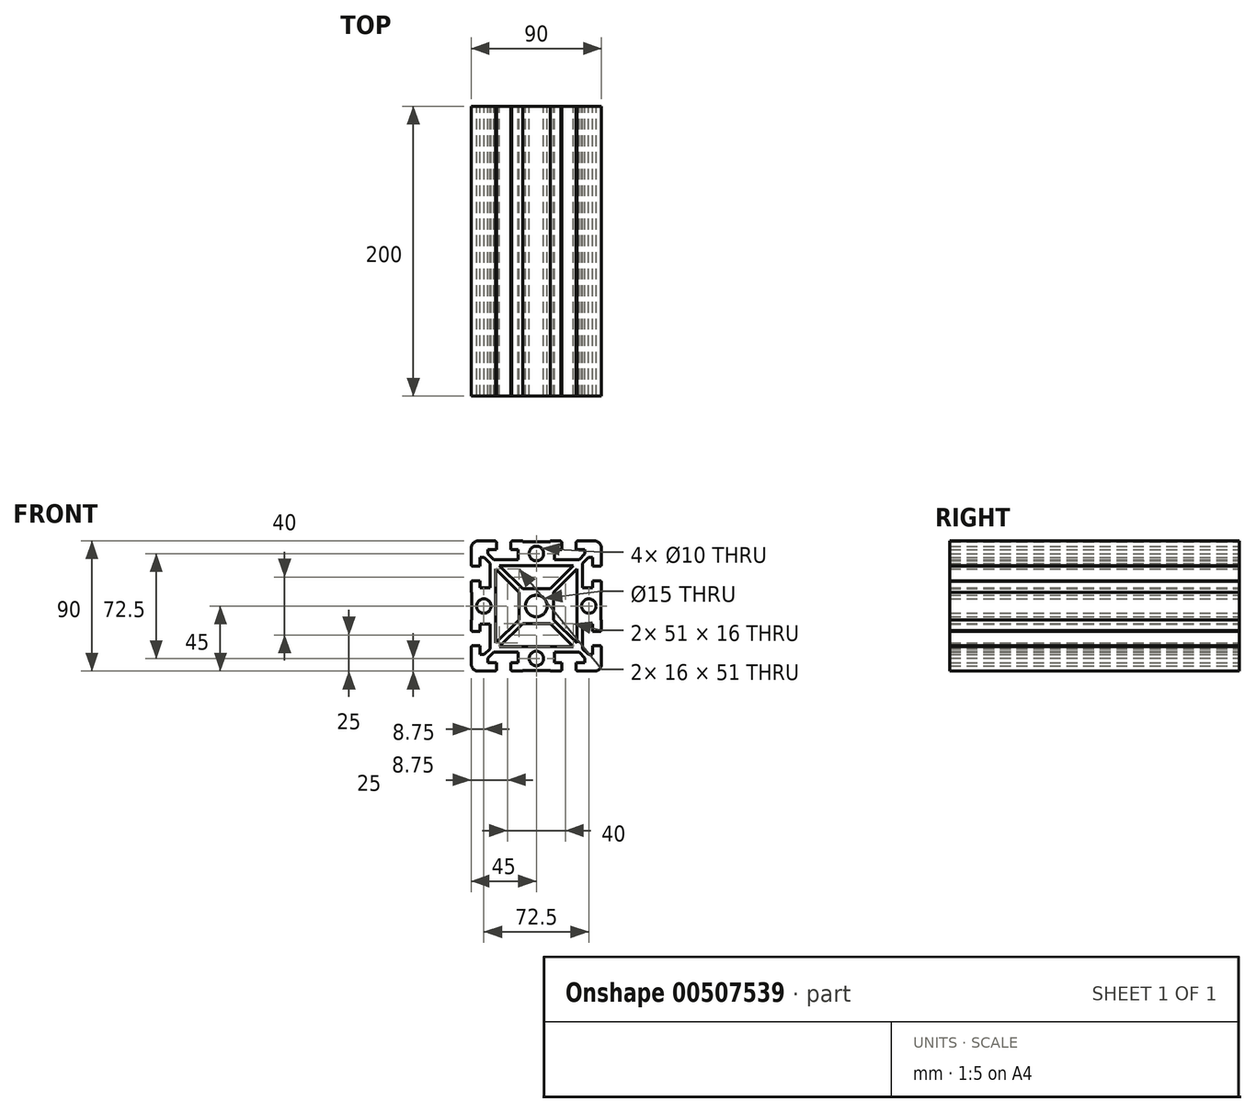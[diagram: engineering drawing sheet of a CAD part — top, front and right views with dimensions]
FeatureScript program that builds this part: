
annotation { "Feature Type Name" : "Feature", "Feature Type Description" : "" }
export const myFeature = defineFeature(function(context is Context, id is Id, definition is map)
    precondition{}
    {
        {
            var Q0;
            Q0=qCreatedBy(makeId("Front.planeOp"),FACE);
            var sketch = newSketch(context, id + "F0", { "sketchPlane" : qUnion([Q0])});
            skLineSegment(sketch, "E0", {"start": v(28, 45) * mm, "end": v(28, 44.5) * mm});
            skLineSegment(sketch, "E1", {"start": v(28, 44.5) * mm, "end": v(27.5, 44.5) * mm});
            skLineSegment(sketch, "E2", {"start": v(27.5, 44.5) * mm, "end": v(27.5, 39) * mm});
            skLineSegment(sketch, "E3", {"start": v(27.5, 39) * mm, "end": v(33.5, 39) * mm});
            skLineSegment(sketch, "E4", {"start": v(33.5, 39) * mm, "end": v(33.5, 36) * mm});
            skLineSegment(sketch, "E5", {"start": v(33.5, 36) * mm, "end": v(29.5, 32) * mm});
            skLineSegment(sketch, "E6", {"start": v(29.5, 32) * mm, "end": v(12.5, 32) * mm});
            skLineSegment(sketch, "E7", {"start": v(12.5, 32) * mm, "end": v(12.5, 39) * mm});
            skLineSegment(sketch, "E8", {"start": v(12.5, 39) * mm, "end": v(17.5, 39) * mm});
            skLineSegment(sketch, "E9", {"start": v(17.5, 39) * mm, "end": v(17.5, 44.5) * mm});
            skLineSegment(sketch, "E10", {"start": v(17.5, 44.5) * mm, "end": v(17, 44.5) * mm});
            skLineSegment(sketch, "E11", {"start": v(17, 44.5) * mm, "end": v(17, 45) * mm});
            skLineSegment(sketch, "E12", {"start": v(45, 28) * mm, "end": v(44.5, 28) * mm});
            skLineSegment(sketch, "E13", {"start": v(44.5, 28) * mm, "end": v(44.5, 27.5) * mm});
            skLineSegment(sketch, "E14", {"start": v(44.5, 27.5) * mm, "end": v(39, 27.5) * mm});
            skLineSegment(sketch, "E15", {"start": v(39, 27.5) * mm, "end": v(39, 33.5) * mm});
            skLineSegment(sketch, "E16", {"start": v(39, 33.5) * mm, "end": v(36, 33.5) * mm});
            skLineSegment(sketch, "E17", {"start": v(36, 33.5) * mm, "end": v(32, 29.5) * mm});
            skLineSegment(sketch, "E18", {"start": v(32, 29.5) * mm, "end": v(32, 12.5) * mm});
            skLineSegment(sketch, "E19", {"start": v(32, 12.5) * mm, "end": v(39, 12.5) * mm});
            skLineSegment(sketch, "E20", {"start": v(39, 12.5) * mm, "end": v(39, 17.5) * mm});
            skLineSegment(sketch, "E21", {"start": v(39, 17.5) * mm, "end": v(44.5, 17.5) * mm});
            skLineSegment(sketch, "E22", {"start": v(44.5, 17.5) * mm, "end": v(44.5, 17) * mm});
            skLineSegment(sketch, "E23", {"start": v(44.5, 17) * mm, "end": v(45, 17) * mm});
            skLineSegment(sketch, "E24", {"start": v(45, 28) * mm, "end": v(45, 40) * mm});
            skLineSegment(sketch, "E25", {"start": v(28, 45) * mm, "end": v(40, 45) * mm});
            skPoint(sketch, "E26.visualSharp", {"position": v(45, 45) * mm});
            skArc(sketch, "E26.filletArc", {"start": v(45, 40) * mm, "mid": v(43.54, 43.54) * mm, "end": v(40, 45) * mm});
            skLineSegment(sketch, "E27", {"start": v(17, 45) * mm, "end": v(9.5, 45) * mm});
            skLineSegment(sketch, "E28", {"start": v(9.5, 45) * mm, "end": v(9.5, 44.5) * mm});
            skLineSegment(sketch, "E29", {"start": v(9.5, 44.5) * mm, "end": v(0, 44.5) * mm});
            skLineSegment(sketch, "E30", {"start": v(0, 44.5) * mm, "end": v(0, 41.25) * mm});
            skLineSegment(sketch, "E31", {"start": v(45, 17) * mm, "end": v(45, 9.5) * mm});
            skLineSegment(sketch, "E32", {"start": v(45, 9.5) * mm, "end": v(44.5, 9.5) * mm});
            skLineSegment(sketch, "E33", {"start": v(44.5, 9.5) * mm, "end": v(44.5, 0) * mm});
            skLineSegment(sketch, "E34", {"start": v(44.5, 0) * mm, "end": v(41.25, 0) * mm});
            skLineSegment(sketch, "E35.bottom", {"start": v(7.5, 0) * mm, "end": v(12, 0) * mm});
            skLineSegment(sketch, "E35.top", {"start": v(0, 28) * mm, "end": v(25.5, 28) * mm});
            skLineSegment(sketch, "E35.right", {"start": v(28, 0) * mm, "end": v(28, 25.5) * mm});
            skLineSegment(sketch, "E36.top", {"start": v(0, 12) * mm, "end": v(9.5, 12) * mm});
            skLineSegment(sketch, "E36.left", {"start": v(0, 7.5) * mm, "end": v(0, 12) * mm});
            skLineSegment(sketch, "E36.right", {"start": v(12, 0) * mm, "end": v(12, 9.5) * mm});
            skArc(sketch, "E37", {"start": v(7.5, 0) * mm, "mid": v(5.3, 5.3) * mm, "end": v(0, 7.5) * mm});
            skLineSegment(sketch, "E38", {"start": v(25.5, 28) * mm, "end": v(9.5, 12) * mm});
            skLineSegment(sketch, "E39", {"start": v(28, 25.5) * mm, "end": v(12, 9.5) * mm});
            skLineSegment(sketch, "E40.trimOffspring", {"start": v(12, 0) * mm, "end": v(7.5, 0) * mm});
            skLineSegment(sketch, "E41.trimOffspring", {"start": v(0, 12) * mm, "end": v(0, 7.5) * mm});
            skArc(sketch, "E42", {"start": v(41.25, 0) * mm, "mid": v(36.25, 5) * mm, "end": v(31.25, 0) * mm});
            skArc(sketch, "E43", {"start": v(0, 31.25) * mm, "mid": v(5, 36.25) * mm, "end": v(0, 41.25) * mm});
            skLineSegment(sketch, "E44.trimOffspring", {"start": v(0, 31.25) * mm, "end": v(0, 28) * mm});
            skLineSegment(sketch, "E45.trimOffspring", {"start": v(31.25, 0) * mm, "end": v(28, 0) * mm});
            skLineSegment(sketch, "E46.1.0", {"start": v(-28, 0) * mm, "end": v(-28, 25.5) * mm});
            skLineSegment(sketch, "E46.1.1", {"start": v(0, 28) * mm, "end": v(-25.5, 28) * mm});
            skPoint(sketch, "E46.1.2", {"position": v(-45, 45) * mm});
            skArc(sketch, "E46.1.3", {"start": v(0, 41.25) * mm, "mid": v(-5, 36.25) * mm, "end": v(0, 31.25) * mm});
            skLineSegment(sketch, "E46.1.4", {"start": v(-25.5, 28) * mm, "end": v(-9.5, 12) * mm});
            skLineSegment(sketch, "E46.1.5", {"start": v(-44.5, 9.5) * mm, "end": v(-44.5, 0) * mm});
            skLineSegment(sketch, "E46.1.6", {"start": v(-28, 25.5) * mm, "end": v(-12, 9.5) * mm});
            skLineSegment(sketch, "E46.1.7", {"start": v(-28, 45) * mm, "end": v(-40, 45) * mm});
            skLineSegment(sketch, "E46.1.8", {"start": v(-32, 29.5) * mm, "end": v(-32, 12.5) * mm});
            skArc(sketch, "E46.1.9", {"start": v(-31.25, 0) * mm, "mid": v(-36.25, 5) * mm, "end": v(-41.25, 0) * mm});
            skLineSegment(sketch, "E46.1.10", {"start": v(-9.5, 44.5) * mm, "end": v(0, 44.5) * mm});
            skLineSegment(sketch, "E46.1.11", {"start": v(-12.5, 32) * mm, "end": v(-12.5, 39) * mm});
            skLineSegment(sketch, "E46.1.12", {"start": v(-12, 0) * mm, "end": v(-12, 9.5) * mm});
            skLineSegment(sketch, "E46.1.13", {"start": v(-45, 17) * mm, "end": v(-45, 9.5) * mm});
            skArc(sketch, "E46.1.14", {"start": v(-40, 45) * mm, "mid": v(-43.54, 43.54) * mm, "end": v(-45, 40) * mm});
            skArc(sketch, "E46.1.15", {"start": v(0, 7.5) * mm, "mid": v(-5.3, 5.3) * mm, "end": v(-7.5, 0) * mm});
            skLineSegment(sketch, "E46.1.16", {"start": v(-45, 28) * mm, "end": v(-45, 40) * mm});
            skLineSegment(sketch, "E46.1.17", {"start": v(0, 12) * mm, "end": v(-9.5, 12) * mm});
            skLineSegment(sketch, "E46.1.18", {"start": v(-17, 45) * mm, "end": v(-9.5, 45) * mm});
            skLineSegment(sketch, "E46.1.19", {"start": v(-32, 12.5) * mm, "end": v(-39, 12.5) * mm});
            skLineSegment(sketch, "E46.1.20", {"start": v(-29.5, 32) * mm, "end": v(-12.5, 32) * mm});
            skLineSegment(sketch, "E46.1.21", {"start": v(-12.5, 39) * mm, "end": v(-17.5, 39) * mm});
            skLineSegment(sketch, "E46.1.22", {"start": v(-17.5, 39) * mm, "end": v(-17.5, 44.5) * mm});
            skLineSegment(sketch, "E46.1.23", {"start": v(-44.5, 0) * mm, "end": v(-41.25, 0) * mm});
            skLineSegment(sketch, "E46.1.24", {"start": v(-27.5, 39) * mm, "end": v(-33.5, 39) * mm});
            skLineSegment(sketch, "E46.1.25", {"start": v(-36, 33.5) * mm, "end": v(-32, 29.5) * mm});
            skLineSegment(sketch, "E46.1.26", {"start": v(-39, 12.5) * mm, "end": v(-39, 17.5) * mm});
            skLineSegment(sketch, "E46.1.27", {"start": v(-39, 17.5) * mm, "end": v(-44.5, 17.5) * mm});
            skLineSegment(sketch, "E46.1.28", {"start": v(-33.5, 39) * mm, "end": v(-33.5, 36) * mm});
            skLineSegment(sketch, "E46.1.29", {"start": v(-33.5, 36) * mm, "end": v(-29.5, 32) * mm});
            skLineSegment(sketch, "E46.1.30", {"start": v(-31.25, 0) * mm, "end": v(-28, 0) * mm});
            skLineSegment(sketch, "E46.1.33", {"start": v(-12, 0) * mm, "end": v(-7.5, 0) * mm});
            skLineSegment(sketch, "E46.1.34", {"start": v(-27.5, 44.5) * mm, "end": v(-27.5, 39) * mm});
            skLineSegment(sketch, "E46.1.35", {"start": v(-44.5, 27.5) * mm, "end": v(-39, 27.5) * mm});
            skLineSegment(sketch, "E46.1.36", {"start": v(-39, 27.5) * mm, "end": v(-39, 33.5) * mm});
            skLineSegment(sketch, "E46.1.37", {"start": v(-39, 33.5) * mm, "end": v(-36, 33.5) * mm});
            skLineSegment(sketch, "E46.1.39", {"start": v(-7.5, 0) * mm, "end": v(-12, 0) * mm});
            skLineSegment(sketch, "E46.1.40", {"start": v(-45, 28) * mm, "end": v(-44.5, 28) * mm});
            skLineSegment(sketch, "E46.1.41", {"start": v(-44.5, 28) * mm, "end": v(-44.5, 27.5) * mm});
            skLineSegment(sketch, "E46.1.42", {"start": v(-9.5, 45) * mm, "end": v(-9.5, 44.5) * mm});
            skLineSegment(sketch, "E46.1.43", {"start": v(-17.5, 44.5) * mm, "end": v(-17, 44.5) * mm});
            skLineSegment(sketch, "E46.1.45", {"start": v(-17, 44.5) * mm, "end": v(-17, 45) * mm});
            skLineSegment(sketch, "E46.1.46", {"start": v(-45, 9.5) * mm, "end": v(-44.5, 9.5) * mm});
            skLineSegment(sketch, "E46.1.47", {"start": v(-44.5, 17) * mm, "end": v(-45, 17) * mm});
            skLineSegment(sketch, "E46.1.49", {"start": v(-44.5, 17.5) * mm, "end": v(-44.5, 17) * mm});
            skLineSegment(sketch, "E46.1.50", {"start": v(-28, 44.5) * mm, "end": v(-27.5, 44.5) * mm});
            skLineSegment(sketch, "E46.1.51", {"start": v(-28, 45) * mm, "end": v(-28, 44.5) * mm});
            skLineSegment(sketch, "E46.2.0", {"start": v(0, -28) * mm, "end": v(-25.5, -28) * mm});
            skLineSegment(sketch, "E46.2.1", {"start": v(-28, 0) * mm, "end": v(-28, -25.5) * mm});
            skPoint(sketch, "E46.2.2", {"position": v(-45, -45) * mm});
            skArc(sketch, "E46.2.3", {"start": v(-41.25, 0) * mm, "mid": v(-36.25, -5) * mm, "end": v(-31.25, 0) * mm});
            skLineSegment(sketch, "E46.2.4", {"start": v(-28, -25.5) * mm, "end": v(-12, -9.5) * mm});
            skLineSegment(sketch, "E46.2.5", {"start": v(-9.5, -44.5) * mm, "end": v(0, -44.5) * mm});
            skLineSegment(sketch, "E46.2.6", {"start": v(-25.5, -28) * mm, "end": v(-9.5, -12) * mm});
            skLineSegment(sketch, "E46.2.7", {"start": v(-45, -28) * mm, "end": v(-45, -40) * mm});
            skLineSegment(sketch, "E46.2.8", {"start": v(-29.5, -32) * mm, "end": v(-12.5, -32) * mm});
            skArc(sketch, "E46.2.9", {"start": v(0, -31.25) * mm, "mid": v(-5, -36.25) * mm, "end": v(0, -41.25) * mm});
            skLineSegment(sketch, "E46.2.10", {"start": v(-44.5, -9.5) * mm, "end": v(-44.5, 0) * mm});
            skLineSegment(sketch, "E46.2.11", {"start": v(-32, -12.5) * mm, "end": v(-39, -12.5) * mm});
            skLineSegment(sketch, "E46.2.12", {"start": v(0, -12) * mm, "end": v(-9.5, -12) * mm});
            skLineSegment(sketch, "E46.2.13", {"start": v(-17, -45) * mm, "end": v(-9.5, -45) * mm});
            skArc(sketch, "E46.2.14", {"start": v(-45, -40) * mm, "mid": v(-43.54, -43.54) * mm, "end": v(-40, -45) * mm});
            skArc(sketch, "E46.2.15", {"start": v(-7.5, 0) * mm, "mid": v(-5.3, -5.3) * mm, "end": v(0, -7.5) * mm});
            skLineSegment(sketch, "E46.2.16", {"start": v(-28, -45) * mm, "end": v(-40, -45) * mm});
            skLineSegment(sketch, "E46.2.17", {"start": v(-12, 0) * mm, "end": v(-12, -9.5) * mm});
            skLineSegment(sketch, "E46.2.18", {"start": v(-45, -17) * mm, "end": v(-45, -9.5) * mm});
            skLineSegment(sketch, "E46.2.19", {"start": v(-12.5, -32) * mm, "end": v(-12.5, -39) * mm});
            skLineSegment(sketch, "E46.2.20", {"start": v(-32, -29.5) * mm, "end": v(-32, -12.5) * mm});
            skLineSegment(sketch, "E46.2.21", {"start": v(-39, -12.5) * mm, "end": v(-39, -17.5) * mm});
            skLineSegment(sketch, "E46.2.22", {"start": v(-39, -17.5) * mm, "end": v(-44.5, -17.5) * mm});
            skLineSegment(sketch, "E46.2.23", {"start": v(0, -44.5) * mm, "end": v(0, -41.25) * mm});
            skLineSegment(sketch, "E46.2.24", {"start": v(-39, -27.5) * mm, "end": v(-39, -33.5) * mm});
            skLineSegment(sketch, "E46.2.25", {"start": v(-33.5, -36) * mm, "end": v(-29.5, -32) * mm});
            skLineSegment(sketch, "E46.2.26", {"start": v(-12.5, -39) * mm, "end": v(-17.5, -39) * mm});
            skLineSegment(sketch, "E46.2.27", {"start": v(-17.5, -39) * mm, "end": v(-17.5, -44.5) * mm});
            skLineSegment(sketch, "E46.2.28", {"start": v(-39, -33.5) * mm, "end": v(-36, -33.5) * mm});
            skLineSegment(sketch, "E46.2.29", {"start": v(-36, -33.5) * mm, "end": v(-32, -29.5) * mm});
            skLineSegment(sketch, "E46.2.30", {"start": v(0, -31.25) * mm, "end": v(0, -28) * mm});
            skLineSegment(sketch, "E46.2.31", {"start": v(-31.25, 0) * mm, "end": v(-28, 0) * mm});
            skLineSegment(sketch, "E46.2.32", {"start": v(-44.5, 0) * mm, "end": v(-41.25, 0) * mm});
            skLineSegment(sketch, "E46.2.33", {"start": v(0, -12) * mm, "end": v(0, -7.5) * mm});
            skLineSegment(sketch, "E46.2.34", {"start": v(-44.5, -27.5) * mm, "end": v(-39, -27.5) * mm});
            skLineSegment(sketch, "E46.2.35", {"start": v(-27.5, -44.5) * mm, "end": v(-27.5, -39) * mm});
            skLineSegment(sketch, "E46.2.36", {"start": v(-27.5, -39) * mm, "end": v(-33.5, -39) * mm});
            skLineSegment(sketch, "E46.2.37", {"start": v(-33.5, -39) * mm, "end": v(-33.5, -36) * mm});
            skLineSegment(sketch, "E46.2.38", {"start": v(-12, 0) * mm, "end": v(-7.5, 0) * mm});
            skLineSegment(sketch, "E46.2.39", {"start": v(0, -7.5) * mm, "end": v(0, -12) * mm});
            skLineSegment(sketch, "E46.2.40", {"start": v(-28, -45) * mm, "end": v(-28, -44.5) * mm});
            skLineSegment(sketch, "E46.2.41", {"start": v(-28, -44.5) * mm, "end": v(-27.5, -44.5) * mm});
            skLineSegment(sketch, "E46.2.42", {"start": v(-45, -9.5) * mm, "end": v(-44.5, -9.5) * mm});
            skLineSegment(sketch, "E46.2.43", {"start": v(-44.5, -17.5) * mm, "end": v(-44.5, -17) * mm});
            skLineSegment(sketch, "E46.2.44", {"start": v(-7.5, 0) * mm, "end": v(-12, 0) * mm});
            skLineSegment(sketch, "E46.2.45", {"start": v(-44.5, -17) * mm, "end": v(-45, -17) * mm});
            skLineSegment(sketch, "E46.2.46", {"start": v(-9.5, -45) * mm, "end": v(-9.5, -44.5) * mm});
            skLineSegment(sketch, "E46.2.47", {"start": v(-17, -44.5) * mm, "end": v(-17, -45) * mm});
            skLineSegment(sketch, "E46.2.48", {"start": v(-7.5, 0) * mm, "end": v(-12, 0) * mm});
            skLineSegment(sketch, "E46.2.49", {"start": v(-17.5, -44.5) * mm, "end": v(-17, -44.5) * mm});
            skLineSegment(sketch, "E46.2.50", {"start": v(-44.5, -28) * mm, "end": v(-44.5, -27.5) * mm});
            skLineSegment(sketch, "E46.2.51", {"start": v(-45, -28) * mm, "end": v(-44.5, -28) * mm});
            skLineSegment(sketch, "E46.3.0", {"start": v(28, 0) * mm, "end": v(28, -25.5) * mm});
            skLineSegment(sketch, "E46.3.1", {"start": v(0, -28) * mm, "end": v(25.5, -28) * mm});
            skPoint(sketch, "E46.3.2", {"position": v(45, -45) * mm});
            skArc(sketch, "E46.3.3", {"start": v(0, -41.25) * mm, "mid": v(5, -36.25) * mm, "end": v(0, -31.25) * mm});
            skLineSegment(sketch, "E46.3.4", {"start": v(25.5, -28) * mm, "end": v(9.5, -12) * mm});
            skLineSegment(sketch, "E46.3.5", {"start": v(44.5, -9.5) * mm, "end": v(44.5, 0) * mm});
            skLineSegment(sketch, "E46.3.6", {"start": v(28, -25.5) * mm, "end": v(12, -9.5) * mm});
            skLineSegment(sketch, "E46.3.7", {"start": v(28, -45) * mm, "end": v(40, -45) * mm});
            skLineSegment(sketch, "E46.3.8", {"start": v(32, -29.5) * mm, "end": v(32, -12.5) * mm});
            skArc(sketch, "E46.3.9", {"start": v(31.25, 0) * mm, "mid": v(36.25, -5) * mm, "end": v(41.25, 0) * mm});
            skLineSegment(sketch, "E46.3.10", {"start": v(9.5, -44.5) * mm, "end": v(0, -44.5) * mm});
            skLineSegment(sketch, "E46.3.11", {"start": v(12.5, -32) * mm, "end": v(12.5, -39) * mm});
            skLineSegment(sketch, "E46.3.12", {"start": v(12, 0) * mm, "end": v(12, -9.5) * mm});
            skLineSegment(sketch, "E46.3.13", {"start": v(45, -17) * mm, "end": v(45, -9.5) * mm});
            skArc(sketch, "E46.3.14", {"start": v(40, -45) * mm, "mid": v(43.54, -43.54) * mm, "end": v(45, -40) * mm});
            skArc(sketch, "E46.3.15", {"start": v(0, -7.5) * mm, "mid": v(5.3, -5.3) * mm, "end": v(7.5, 0) * mm});
            skLineSegment(sketch, "E46.3.16", {"start": v(45, -28) * mm, "end": v(45, -40) * mm});
            skLineSegment(sketch, "E46.3.17", {"start": v(0, -12) * mm, "end": v(9.5, -12) * mm});
            skLineSegment(sketch, "E46.3.18", {"start": v(17, -45) * mm, "end": v(9.5, -45) * mm});
            skLineSegment(sketch, "E46.3.19", {"start": v(32, -12.5) * mm, "end": v(39, -12.5) * mm});
            skLineSegment(sketch, "E46.3.20", {"start": v(29.5, -32) * mm, "end": v(12.5, -32) * mm});
            skLineSegment(sketch, "E46.3.21", {"start": v(12.5, -39) * mm, "end": v(17.5, -39) * mm});
            skLineSegment(sketch, "E46.3.22", {"start": v(17.5, -39) * mm, "end": v(17.5, -44.5) * mm});
            skLineSegment(sketch, "E46.3.24", {"start": v(27.5, -39) * mm, "end": v(33.5, -39) * mm});
            skLineSegment(sketch, "E46.3.25", {"start": v(36, -33.5) * mm, "end": v(32, -29.5) * mm});
            skLineSegment(sketch, "E46.3.26", {"start": v(39, -12.5) * mm, "end": v(39, -17.5) * mm});
            skLineSegment(sketch, "E46.3.27", {"start": v(39, -17.5) * mm, "end": v(44.5, -17.5) * mm});
            skLineSegment(sketch, "E46.3.28", {"start": v(33.5, -39) * mm, "end": v(33.5, -36) * mm});
            skLineSegment(sketch, "E46.3.29", {"start": v(33.5, -36) * mm, "end": v(29.5, -32) * mm});
            skLineSegment(sketch, "E46.3.31", {"start": v(0, -31.25) * mm, "end": v(0, -28) * mm});
            skLineSegment(sketch, "E46.3.32", {"start": v(0, -44.5) * mm, "end": v(0, -41.25) * mm});
            skLineSegment(sketch, "E46.3.34", {"start": v(27.5, -44.5) * mm, "end": v(27.5, -39) * mm});
            skLineSegment(sketch, "E46.3.35", {"start": v(44.5, -27.5) * mm, "end": v(39, -27.5) * mm});
            skLineSegment(sketch, "E46.3.36", {"start": v(39, -27.5) * mm, "end": v(39, -33.5) * mm});
            skLineSegment(sketch, "E46.3.37", {"start": v(39, -33.5) * mm, "end": v(36, -33.5) * mm});
            skLineSegment(sketch, "E46.3.38", {"start": v(0, -12) * mm, "end": v(0, -7.5) * mm});
            skLineSegment(sketch, "E46.3.40", {"start": v(45, -28) * mm, "end": v(44.5, -28) * mm});
            skLineSegment(sketch, "E46.3.41", {"start": v(44.5, -28) * mm, "end": v(44.5, -27.5) * mm});
            skLineSegment(sketch, "E46.3.42", {"start": v(9.5, -45) * mm, "end": v(9.5, -44.5) * mm});
            skLineSegment(sketch, "E46.3.43", {"start": v(17.5, -44.5) * mm, "end": v(17, -44.5) * mm});
            skLineSegment(sketch, "E46.3.44", {"start": v(0, -7.5) * mm, "end": v(0, -12) * mm});
            skLineSegment(sketch, "E46.3.45", {"start": v(17, -44.5) * mm, "end": v(17, -45) * mm});
            skLineSegment(sketch, "E46.3.46", {"start": v(45, -9.5) * mm, "end": v(44.5, -9.5) * mm});
            skLineSegment(sketch, "E46.3.47", {"start": v(44.5, -17) * mm, "end": v(45, -17) * mm});
            skLineSegment(sketch, "E46.3.48", {"start": v(0, -7.5) * mm, "end": v(0, -12) * mm});
            skLineSegment(sketch, "E46.3.49", {"start": v(44.5, -17.5) * mm, "end": v(44.5, -17) * mm});
            skLineSegment(sketch, "E46.3.50", {"start": v(28, -44.5) * mm, "end": v(27.5, -44.5) * mm});
            skLineSegment(sketch, "E46.3.51", {"start": v(28, -45) * mm, "end": v(28, -44.5) * mm});
            skPoint(sketch, "E46.center", {"position": v(0, 0) * mm});
            skLineSegment(sketch, "E47", {"start": v(-165.83, 16.5) * mm, "end": v(-157.83, 16.5) * mm});
            skLineSegment(sketch, "E48", {"start": v(-157.83, 16.5) * mm, "end": v(-157.83, 17) * mm});
            skLineSegment(sketch, "E49", {"start": v(-157.83, 17) * mm, "end": v(-148.83, 17) * mm});
            skLineSegment(sketch, "E50", {"start": v(-148.83, 17) * mm, "end": v(-148.83, 16.5) * mm});
            skLineSegment(sketch, "E51", {"start": v(-148.83, 16.5) * mm, "end": v(-148.33, 16.5) * mm});
            skLineSegment(sketch, "E52", {"start": v(-148.33, 16.5) * mm, "end": v(-148.33, 11) * mm});
            skLineSegment(sketch, "E53", {"start": v(-148.33, 11) * mm, "end": v(-154.83, 11) * mm});
            skLineSegment(sketch, "E54", {"start": v(-154.83, 11) * mm, "end": v(-154.83, 4) * mm});
            skLineSegment(sketch, "E55", {"start": v(-154.83, 4) * mm, "end": v(-135.95, 4) * mm});
            skLineSegment(sketch, "E56", {"start": v(-135.95, 4) * mm, "end": v(-131.83, 8.12) * mm});
            skLineSegment(sketch, "E57", {"start": v(-131.83, 8.12) * mm, "end": v(-131.83, 11) * mm});
            skLineSegment(sketch, "E58", {"start": v(-131.83, 11) * mm, "end": v(-138.33, 11) * mm});
            skLineSegment(sketch, "E59", {"start": v(-138.33, 11) * mm, "end": v(-138.33, 16.5) * mm});
            skLineSegment(sketch, "E60", {"start": v(-138.33, 16.5) * mm, "end": v(-137.83, 16.5) * mm});
            skLineSegment(sketch, "E61", {"start": v(-137.83, 16.5) * mm, "end": v(-137.83, 17) * mm});
            skLineSegment(sketch, "E62", {"start": v(-137.83, 17) * mm, "end": v(-125.83, 17) * mm});
            skArc(sketch, "E63", {"start": v(-125.83, 17) * mm, "mid": v(-123.92, 16.62) * mm, "end": v(-122.3, 15.54) * mm});
            skLineSegment(sketch, "E64", {"start": v(-165.83, 10.5) * mm, "end": v(-163.87, 10.5) * mm});
            skLineSegment(sketch, "E65", {"start": v(-163.87, 10.5) * mm, "end": v(-163.87, 9.5) * mm});
            skArc(sketch, "E66", {"start": v(-163.87, 9.5) * mm, "mid": v(-160.93, 5.88) * mm, "end": v(-162.26, 1.4) * mm});
            skArc(sketch, "E67", {"start": v(-162.26, 1.4) * mm, "mid": v(-162.67, -0.77) * mm, "end": v(-160.83, -2) * mm});
            skLineSegment(sketch, "E68", {"start": v(-160.83, -2) * mm, "end": v(-146.78, -2) * mm});
            skArc(sketch, "E69", {"start": v(-146.78, -2) * mm, "mid": v(-144.93, -3.23) * mm, "end": v(-145.37, -5.41) * mm});
            skLineSegment(sketch, "E70", {"start": v(-145.37, -5.41) * mm, "end": v(-154.45, -14.5) * mm});
            skLineSegment(sketch, "E71", {"start": v(-154.45, -14.5) * mm, "end": v(-165.83, -14.5) * mm});
            skArc(sketch, "E72", {"start": v(-165.83, -20.5) * mm, "mid": v(-162.96, -21.07) * mm, "end": v(-160.53, -22.7) * mm});
            skLineSegment(sketch, "E73", {"start": v(-160.53, -22.7) * mm, "end": v(-165.83, -28) * mm, "construction": true});
            skLineSegment(sketch, "E74", {"start": v(-165.83, -20.5) * mm, "end": v(-165.83, -28) * mm, "construction": true});
            skLineSegment(sketch, "E75.MirrorCS", {"start": v(-121.33, -0.5) * mm, "end": v(-121.33, 0) * mm});
            skLineSegment(sketch, "E76.MirrorCS", {"start": v(-129.7, 6) * mm, "end": v(-126.83, 6) * mm});
            skLineSegment(sketch, "E77.MirrorCS", {"start": v(-121.33, -11) * mm, "end": v(-121.33, -10.5) * mm});
            skLineSegment(sketch, "E78.MirrorCS", {"start": v(-120.83, -11) * mm, "end": v(-121.33, -11) * mm});
            skLineSegment(sketch, "E79.MirrorCS", {"start": v(-127.33, -26.04) * mm, "end": v(-128.33, -26.04) * mm});
            skLineSegment(sketch, "E80.MirrorCS", {"start": v(-121.33, -20) * mm, "end": v(-120.83, -20) * mm});
            skLineSegment(sketch, "E81.MirrorCS", {"start": v(-121.33, 0) * mm, "end": v(-120.83, 0) * mm});
            skArc(sketch, "E82.MirrorCS", {"start": v(-136.43, -24.43) * mm, "mid": v(-138.6, -24.84) * mm, "end": v(-139.83, -23) * mm});
            skLineSegment(sketch, "E83.MirrorCS", {"start": v(-127.33, -28) * mm, "end": v(-127.33, -26.04) * mm});
            skArc(sketch, "E84.MirrorCS", {"start": v(-120.83, 12) * mm, "mid": v(-121.21, 13.91) * mm, "end": v(-122.3, 15.54) * mm});
            skLineSegment(sketch, "E85.MirrorCS", {"start": v(-126.83, -0.5) * mm, "end": v(-121.33, -0.5) * mm});
            skArc(sketch, "E86.MirrorCS", {"start": v(-158.33, -28) * mm, "mid": v(-158.9, -25.13) * mm, "end": v(-160.53, -22.7) * mm});
            skLineSegment(sketch, "E87.MirrorCS", {"start": v(-133.83, 1.88) * mm, "end": v(-129.7, 6) * mm});
            skLineSegment(sketch, "E88.MirrorCS", {"start": v(-152.33, -16.62) * mm, "end": v(-152.33, -28) * mm});
            skLineSegment(sketch, "E89.MirrorCS", {"start": v(-133.83, -17) * mm, "end": v(-133.83, 1.88) * mm});
            skLineSegment(sketch, "E90.MirrorCS", {"start": v(-143.25, -7.54) * mm, "end": v(-152.33, -16.62) * mm});
            skLineSegment(sketch, "E91.MirrorCS", {"start": v(-126.83, -17) * mm, "end": v(-133.83, -17) * mm});
            skLineSegment(sketch, "E92.MirrorCS", {"start": v(-126.83, -10.5) * mm, "end": v(-126.83, -17) * mm});
            skArc(sketch, "E93.MirrorCS", {"start": v(-139.83, -8.95) * mm, "mid": v(-141.07, -7.1) * mm, "end": v(-143.25, -7.54) * mm});
            skLineSegment(sketch, "E94.MirrorCS", {"start": v(-121.33, -10.5) * mm, "end": v(-126.83, -10.5) * mm});
            skLineSegment(sketch, "E95.MirrorCS", {"start": v(-139.83, -23) * mm, "end": v(-139.83, -8.95) * mm});
            skArc(sketch, "E96.MirrorCS", {"start": v(-128.33, -26.04) * mm, "mid": v(-131.95, -23.1) * mm, "end": v(-136.43, -24.43) * mm});
            skLineSegment(sketch, "E97.MirrorCS", {"start": v(-120.83, -20) * mm, "end": v(-120.83, -11) * mm});
            skLineSegment(sketch, "E98.MirrorCS", {"start": v(-121.33, -28) * mm, "end": v(-121.33, -20) * mm});
            skLineSegment(sketch, "E99.MirrorCS", {"start": v(-120.83, 0) * mm, "end": v(-120.83, 12) * mm});
            skLineSegment(sketch, "E100.MirrorCS", {"start": v(-126.83, 6) * mm, "end": v(-126.83, -0.5) * mm});
            skLineSegment(sketch, "E101.MirrorCS", {"start": v(-158.33, -28) * mm, "end": v(-165.83, -28) * mm, "construction": true});
            skArc(sketch, "E102.1.0", {"start": v(-158.33, -28) * mm, "mid": v(-158.9, -30.87) * mm, "end": v(-160.53, -33.3) * mm});
            skLineSegment(sketch, "E102.1.1", {"start": v(-133.83, -57.88) * mm, "end": v(-129.7, -62) * mm});
            skArc(sketch, "E102.1.2", {"start": v(-128.33, -29.96) * mm, "mid": v(-131.95, -32.9) * mm, "end": v(-136.43, -31.57) * mm});
            skLineSegment(sketch, "E102.1.3", {"start": v(-165.83, -72.5) * mm, "end": v(-157.83, -72.5) * mm});
            skLineSegment(sketch, "E102.1.4", {"start": v(-120.83, -36) * mm, "end": v(-120.83, -45) * mm});
            skLineSegment(sketch, "E102.1.5", {"start": v(-121.33, -28) * mm, "end": v(-121.33, -36) * mm});
            skLineSegment(sketch, "E102.1.6", {"start": v(-148.33, -72.5) * mm, "end": v(-148.33, -67) * mm});
            skLineSegment(sketch, "E102.1.8", {"start": v(-154.45, -41.5) * mm, "end": v(-165.83, -41.5) * mm});
            skLineSegment(sketch, "E102.1.9", {"start": v(-154.83, -67) * mm, "end": v(-154.83, -60) * mm});
            skLineSegment(sketch, "E102.1.10", {"start": v(-126.83, -55.5) * mm, "end": v(-121.33, -55.5) * mm});
            skLineSegment(sketch, "E102.1.11", {"start": v(-148.33, -67) * mm, "end": v(-154.83, -67) * mm});
            skLineSegment(sketch, "E102.1.12", {"start": v(-154.83, -60) * mm, "end": v(-135.95, -60) * mm});
            skLineSegment(sketch, "E102.1.13", {"start": v(-160.53, -33.3) * mm, "end": v(-165.83, -28) * mm, "construction": true});
            skLineSegment(sketch, "E102.1.14", {"start": v(-145.37, -50.59) * mm, "end": v(-154.45, -41.5) * mm});
            skLineSegment(sketch, "E102.1.15", {"start": v(-126.83, -62) * mm, "end": v(-126.83, -55.5) * mm});
            skLineSegment(sketch, "E102.1.16", {"start": v(-152.33, -39.38) * mm, "end": v(-152.33, -28) * mm});
            skLineSegment(sketch, "E102.1.17", {"start": v(-135.95, -60) * mm, "end": v(-131.83, -64.12) * mm});
            skLineSegment(sketch, "E102.1.18", {"start": v(-133.83, -39) * mm, "end": v(-133.83, -57.88) * mm});
            skLineSegment(sketch, "E102.1.19", {"start": v(-143.25, -48.46) * mm, "end": v(-152.33, -39.38) * mm});
            skLineSegment(sketch, "E102.1.20", {"start": v(-126.83, -39) * mm, "end": v(-133.83, -39) * mm});
            skLineSegment(sketch, "E102.1.21", {"start": v(-139.83, -33) * mm, "end": v(-139.83, -47.05) * mm});
            skLineSegment(sketch, "E102.1.22", {"start": v(-121.33, -45.5) * mm, "end": v(-126.83, -45.5) * mm});
            skLineSegment(sketch, "E102.1.23", {"start": v(-137.83, -73) * mm, "end": v(-125.83, -73) * mm});
            skLineSegment(sketch, "E102.1.24", {"start": v(-160.83, -54) * mm, "end": v(-146.78, -54) * mm});
            skLineSegment(sketch, "E102.1.25", {"start": v(-157.83, -73) * mm, "end": v(-148.83, -73) * mm});
            skLineSegment(sketch, "E102.1.26", {"start": v(-120.83, -56) * mm, "end": v(-120.83, -68) * mm});
            skArc(sketch, "E102.1.27", {"start": v(-163.87, -65.5) * mm, "mid": v(-160.93, -61.88) * mm, "end": v(-162.26, -57.4) * mm});
            skLineSegment(sketch, "E102.1.28", {"start": v(-131.83, -67) * mm, "end": v(-138.33, -67) * mm});
            skLineSegment(sketch, "E102.1.29", {"start": v(-138.33, -67) * mm, "end": v(-138.33, -72.5) * mm});
            skLineSegment(sketch, "E102.1.30", {"start": v(-126.83, -45.5) * mm, "end": v(-126.83, -39) * mm});
            skArc(sketch, "E102.1.31", {"start": v(-165.83, -35.5) * mm, "mid": v(-162.96, -34.93) * mm, "end": v(-160.53, -33.3) * mm});
            skLineSegment(sketch, "E102.1.32", {"start": v(-165.83, -35.5) * mm, "end": v(-165.83, -28) * mm, "construction": true});
            skLineSegment(sketch, "E102.1.33", {"start": v(-121.33, -45) * mm, "end": v(-121.33, -45.5) * mm});
            skArc(sketch, "E102.1.34", {"start": v(-162.26, -57.4) * mm, "mid": v(-162.67, -55.23) * mm, "end": v(-160.83, -54) * mm});
            skArc(sketch, "E102.1.35", {"start": v(-120.83, -68) * mm, "mid": v(-121.21, -69.91) * mm, "end": v(-122.3, -71.54) * mm});
            skLineSegment(sketch, "E102.1.36", {"start": v(-163.87, -66.5) * mm, "end": v(-163.87, -65.5) * mm});
            skArc(sketch, "E102.1.37", {"start": v(-146.78, -54) * mm, "mid": v(-144.93, -52.77) * mm, "end": v(-145.37, -50.59) * mm});
            skLineSegment(sketch, "E102.1.38", {"start": v(-131.83, -64.12) * mm, "end": v(-131.83, -67) * mm});
            skLineSegment(sketch, "E102.1.39", {"start": v(-148.83, -72.5) * mm, "end": v(-148.33, -72.5) * mm});
            skLineSegment(sketch, "E102.1.40", {"start": v(-129.7, -62) * mm, "end": v(-126.83, -62) * mm});
            skLineSegment(sketch, "E102.1.41", {"start": v(-165.83, -66.5) * mm, "end": v(-163.87, -66.5) * mm});
            skArc(sketch, "E102.1.42", {"start": v(-136.43, -31.57) * mm, "mid": v(-138.6, -31.16) * mm, "end": v(-139.83, -33) * mm});
            skArc(sketch, "E102.1.43", {"start": v(-125.83, -73) * mm, "mid": v(-123.92, -72.62) * mm, "end": v(-122.3, -71.54) * mm});
            skLineSegment(sketch, "E102.1.44", {"start": v(-127.33, -29.96) * mm, "end": v(-128.33, -29.96) * mm});
            skLineSegment(sketch, "E102.1.45", {"start": v(-148.83, -73) * mm, "end": v(-148.83, -72.5) * mm});
            skLineSegment(sketch, "E102.1.46", {"start": v(-157.83, -72.5) * mm, "end": v(-157.83, -73) * mm});
            skLineSegment(sketch, "E102.1.47", {"start": v(-127.33, -28) * mm, "end": v(-127.33, -29.96) * mm});
            skArc(sketch, "E102.1.48", {"start": v(-139.83, -47.05) * mm, "mid": v(-141.07, -48.9) * mm, "end": v(-143.25, -48.46) * mm});
            skLineSegment(sketch, "E102.1.49", {"start": v(-120.83, -45) * mm, "end": v(-121.33, -45) * mm});
            skLineSegment(sketch, "E102.1.50", {"start": v(-121.33, -36) * mm, "end": v(-120.83, -36) * mm});
            skLineSegment(sketch, "E102.1.51", {"start": v(-121.33, -55.5) * mm, "end": v(-121.33, -56) * mm});
            skLineSegment(sketch, "E102.1.52", {"start": v(-121.33, -56) * mm, "end": v(-120.83, -56) * mm});
            skLineSegment(sketch, "E102.1.53", {"start": v(-138.33, -72.5) * mm, "end": v(-137.83, -72.5) * mm});
            skLineSegment(sketch, "E102.1.54", {"start": v(-137.83, -72.5) * mm, "end": v(-137.83, -73) * mm});
            skArc(sketch, "E102.2.0", {"start": v(-165.83, -35.5) * mm, "mid": v(-168.7, -34.93) * mm, "end": v(-171.13, -33.3) * mm});
            skLineSegment(sketch, "E102.2.1", {"start": v(-195.7, -60) * mm, "end": v(-199.83, -64.12) * mm});
            skArc(sketch, "E102.2.2", {"start": v(-167.79, -65.5) * mm, "mid": v(-170.73, -61.88) * mm, "end": v(-169.4, -57.4) * mm});
            skLineSegment(sketch, "E102.2.3", {"start": v(-210.33, -28) * mm, "end": v(-210.33, -36) * mm});
            skLineSegment(sketch, "E102.2.4", {"start": v(-173.83, -73) * mm, "end": v(-182.83, -73) * mm});
            skLineSegment(sketch, "E102.2.5", {"start": v(-165.83, -72.5) * mm, "end": v(-173.83, -72.5) * mm});
            skLineSegment(sketch, "E102.2.6", {"start": v(-210.33, -45.5) * mm, "end": v(-204.83, -45.5) * mm});
            skLineSegment(sketch, "E102.2.7", {"start": v(-165.83, -35.5) * mm, "end": v(-165.83, -28) * mm, "construction": true});
            skLineSegment(sketch, "E102.2.8", {"start": v(-179.33, -39.38) * mm, "end": v(-179.33, -28) * mm});
            skLineSegment(sketch, "E102.2.9", {"start": v(-204.83, -39) * mm, "end": v(-197.83, -39) * mm});
            skLineSegment(sketch, "E102.2.10", {"start": v(-193.33, -67) * mm, "end": v(-193.33, -72.5) * mm});
            skLineSegment(sketch, "E102.2.11", {"start": v(-204.83, -45.5) * mm, "end": v(-204.83, -39) * mm});
            skLineSegment(sketch, "E102.2.12", {"start": v(-197.83, -39) * mm, "end": v(-197.83, -57.88) * mm});
            skLineSegment(sketch, "E102.2.13", {"start": v(-171.13, -33.3) * mm, "end": v(-165.83, -28) * mm, "construction": true});
            skLineSegment(sketch, "E102.2.14", {"start": v(-188.42, -48.46) * mm, "end": v(-179.33, -39.38) * mm});
            skLineSegment(sketch, "E102.2.15", {"start": v(-199.83, -67) * mm, "end": v(-193.33, -67) * mm});
            skLineSegment(sketch, "E102.2.16", {"start": v(-177.2, -41.5) * mm, "end": v(-165.83, -41.5) * mm});
            skLineSegment(sketch, "E102.2.17", {"start": v(-197.83, -57.88) * mm, "end": v(-201.95, -62) * mm});
            skLineSegment(sketch, "E102.2.18", {"start": v(-176.83, -60) * mm, "end": v(-195.7, -60) * mm});
            skLineSegment(sketch, "E102.2.19", {"start": v(-186.3, -50.59) * mm, "end": v(-177.2, -41.5) * mm});
            skLineSegment(sketch, "E102.2.20", {"start": v(-176.83, -67) * mm, "end": v(-176.83, -60) * mm});
            skLineSegment(sketch, "E102.2.21", {"start": v(-170.83, -54) * mm, "end": v(-184.88, -54) * mm});
            skLineSegment(sketch, "E102.2.22", {"start": v(-183.33, -72.5) * mm, "end": v(-183.33, -67) * mm});
            skLineSegment(sketch, "E102.2.23", {"start": v(-210.83, -56) * mm, "end": v(-210.83, -68) * mm});
            skLineSegment(sketch, "E102.2.24", {"start": v(-191.83, -33) * mm, "end": v(-191.83, -47.05) * mm});
            skLineSegment(sketch, "E102.2.25", {"start": v(-210.83, -36) * mm, "end": v(-210.83, -45) * mm});
            skLineSegment(sketch, "E102.2.26", {"start": v(-193.83, -73) * mm, "end": v(-205.83, -73) * mm});
            skArc(sketch, "E102.2.27", {"start": v(-203.33, -29.96) * mm, "mid": v(-199.7, -32.9) * mm, "end": v(-195.23, -31.57) * mm});
            skLineSegment(sketch, "E102.2.28", {"start": v(-204.83, -62) * mm, "end": v(-204.83, -55.5) * mm});
            skLineSegment(sketch, "E102.2.29", {"start": v(-204.83, -55.5) * mm, "end": v(-210.33, -55.5) * mm});
            skLineSegment(sketch, "E102.2.30", {"start": v(-183.33, -67) * mm, "end": v(-176.83, -67) * mm});
            skArc(sketch, "E102.2.31", {"start": v(-173.33, -28) * mm, "mid": v(-172.76, -30.87) * mm, "end": v(-171.13, -33.3) * mm});
            skLineSegment(sketch, "E102.2.32", {"start": v(-173.33, -28) * mm, "end": v(-165.83, -28) * mm, "construction": true});
            skLineSegment(sketch, "E102.2.33", {"start": v(-182.83, -72.5) * mm, "end": v(-183.33, -72.5) * mm});
            skArc(sketch, "E102.2.34", {"start": v(-195.23, -31.57) * mm, "mid": v(-193.06, -31.16) * mm, "end": v(-191.83, -33) * mm});
            skArc(sketch, "E102.2.35", {"start": v(-205.83, -73) * mm, "mid": v(-207.74, -72.62) * mm, "end": v(-209.37, -71.54) * mm});
            skLineSegment(sketch, "E102.2.36", {"start": v(-204.33, -29.96) * mm, "end": v(-203.33, -29.96) * mm});
            skArc(sketch, "E102.2.37", {"start": v(-191.83, -47.05) * mm, "mid": v(-190.6, -48.9) * mm, "end": v(-188.42, -48.46) * mm});
            skLineSegment(sketch, "E102.2.38", {"start": v(-201.95, -62) * mm, "end": v(-204.83, -62) * mm});
            skLineSegment(sketch, "E102.2.39", {"start": v(-210.33, -45) * mm, "end": v(-210.33, -45.5) * mm});
            skLineSegment(sketch, "E102.2.40", {"start": v(-199.83, -64.12) * mm, "end": v(-199.83, -67) * mm});
            skLineSegment(sketch, "E102.2.41", {"start": v(-204.33, -28) * mm, "end": v(-204.33, -29.96) * mm});
            skArc(sketch, "E102.2.42", {"start": v(-169.4, -57.4) * mm, "mid": v(-168.99, -55.23) * mm, "end": v(-170.83, -54) * mm});
            skArc(sketch, "E102.2.43", {"start": v(-210.83, -68) * mm, "mid": v(-210.45, -69.91) * mm, "end": v(-209.37, -71.54) * mm});
            skLineSegment(sketch, "E102.2.44", {"start": v(-167.79, -66.5) * mm, "end": v(-167.79, -65.5) * mm});
            skLineSegment(sketch, "E102.2.45", {"start": v(-210.83, -45) * mm, "end": v(-210.33, -45) * mm});
            skLineSegment(sketch, "E102.2.46", {"start": v(-210.33, -36) * mm, "end": v(-210.83, -36) * mm});
            skLineSegment(sketch, "E102.2.47", {"start": v(-165.83, -66.5) * mm, "end": v(-167.79, -66.5) * mm});
            skArc(sketch, "E102.2.48", {"start": v(-184.88, -54) * mm, "mid": v(-186.73, -52.77) * mm, "end": v(-186.3, -50.59) * mm});
            skLineSegment(sketch, "E102.2.49", {"start": v(-182.83, -73) * mm, "end": v(-182.83, -72.5) * mm});
            skLineSegment(sketch, "E102.2.50", {"start": v(-173.83, -72.5) * mm, "end": v(-173.83, -73) * mm});
            skLineSegment(sketch, "E102.2.51", {"start": v(-193.33, -72.5) * mm, "end": v(-193.83, -72.5) * mm});
            skLineSegment(sketch, "E102.2.52", {"start": v(-193.83, -72.5) * mm, "end": v(-193.83, -73) * mm});
            skLineSegment(sketch, "E102.2.53", {"start": v(-210.33, -55.5) * mm, "end": v(-210.33, -56) * mm});
            skLineSegment(sketch, "E102.2.54", {"start": v(-210.33, -56) * mm, "end": v(-210.83, -56) * mm});
            skArc(sketch, "E102.3.0", {"start": v(-173.33, -28) * mm, "mid": v(-172.76, -25.13) * mm, "end": v(-171.13, -22.7) * mm});
            skLineSegment(sketch, "E102.3.1", {"start": v(-197.83, 1.88) * mm, "end": v(-201.95, 6) * mm});
            skArc(sketch, "E102.3.2", {"start": v(-203.33, -26.04) * mm, "mid": v(-199.7, -23.1) * mm, "end": v(-195.23, -24.43) * mm});
            skLineSegment(sketch, "E102.3.3", {"start": v(-165.83, 16.5) * mm, "end": v(-173.83, 16.5) * mm});
            skLineSegment(sketch, "E102.3.4", {"start": v(-210.83, -20) * mm, "end": v(-210.83, -11) * mm});
            skLineSegment(sketch, "E102.3.5", {"start": v(-210.33, -28) * mm, "end": v(-210.33, -20) * mm});
            skLineSegment(sketch, "E102.3.6", {"start": v(-183.33, 16.5) * mm, "end": v(-183.33, 11) * mm});
            skLineSegment(sketch, "E102.3.7", {"start": v(-173.33, -28) * mm, "end": v(-165.83, -28) * mm, "construction": true});
            skLineSegment(sketch, "E102.3.8", {"start": v(-177.2, -14.5) * mm, "end": v(-165.83, -14.5) * mm});
            skLineSegment(sketch, "E102.3.9", {"start": v(-176.83, 11) * mm, "end": v(-176.83, 4) * mm});
            skLineSegment(sketch, "E102.3.10", {"start": v(-204.83, -0.5) * mm, "end": v(-210.33, -0.5) * mm});
            skLineSegment(sketch, "E102.3.11", {"start": v(-183.33, 11) * mm, "end": v(-176.83, 11) * mm});
            skLineSegment(sketch, "E102.3.12", {"start": v(-176.83, 4) * mm, "end": v(-195.7, 4) * mm});
            skLineSegment(sketch, "E102.3.13", {"start": v(-171.13, -22.7) * mm, "end": v(-165.83, -28) * mm, "construction": true});
            skLineSegment(sketch, "E102.3.14", {"start": v(-186.3, -5.41) * mm, "end": v(-177.2, -14.5) * mm});
            skLineSegment(sketch, "E102.3.15", {"start": v(-204.83, 6) * mm, "end": v(-204.83, -0.5) * mm});
            skLineSegment(sketch, "E102.3.16", {"start": v(-179.33, -16.62) * mm, "end": v(-179.33, -28) * mm});
            skLineSegment(sketch, "E102.3.17", {"start": v(-195.7, 4) * mm, "end": v(-199.83, 8.12) * mm});
            skLineSegment(sketch, "E102.3.18", {"start": v(-197.83, -17) * mm, "end": v(-197.83, 1.88) * mm});
            skLineSegment(sketch, "E102.3.19", {"start": v(-188.42, -7.54) * mm, "end": v(-179.33, -16.62) * mm});
            skLineSegment(sketch, "E102.3.20", {"start": v(-204.83, -17) * mm, "end": v(-197.83, -17) * mm});
            skLineSegment(sketch, "E102.3.21", {"start": v(-191.83, -23) * mm, "end": v(-191.83, -8.95) * mm});
            skLineSegment(sketch, "E102.3.22", {"start": v(-210.33, -10.5) * mm, "end": v(-204.83, -10.5) * mm});
            skLineSegment(sketch, "E102.3.23", {"start": v(-193.83, 17) * mm, "end": v(-205.83, 17) * mm});
            skLineSegment(sketch, "E102.3.24", {"start": v(-170.83, -2) * mm, "end": v(-184.88, -2) * mm});
            skLineSegment(sketch, "E102.3.25", {"start": v(-173.83, 17) * mm, "end": v(-182.83, 17) * mm});
            skLineSegment(sketch, "E102.3.26", {"start": v(-210.83, 0) * mm, "end": v(-210.83, 12) * mm});
            skArc(sketch, "E102.3.27", {"start": v(-167.79, 9.5) * mm, "mid": v(-170.73, 5.88) * mm, "end": v(-169.4, 1.4) * mm});
            skLineSegment(sketch, "E102.3.28", {"start": v(-199.83, 11) * mm, "end": v(-193.33, 11) * mm});
            skLineSegment(sketch, "E102.3.29", {"start": v(-193.33, 11) * mm, "end": v(-193.33, 16.5) * mm});
            skLineSegment(sketch, "E102.3.30", {"start": v(-204.83, -10.5) * mm, "end": v(-204.83, -17) * mm});
            skArc(sketch, "E102.3.31", {"start": v(-165.83, -20.5) * mm, "mid": v(-168.7, -21.07) * mm, "end": v(-171.13, -22.7) * mm});
            skLineSegment(sketch, "E102.3.33", {"start": v(-210.33, -11) * mm, "end": v(-210.33, -10.5) * mm});
            skArc(sketch, "E102.3.34", {"start": v(-169.4, 1.4) * mm, "mid": v(-168.99, -0.77) * mm, "end": v(-170.83, -2) * mm});
            skArc(sketch, "E102.3.35", {"start": v(-210.83, 12) * mm, "mid": v(-210.45, 13.91) * mm, "end": v(-209.37, 15.54) * mm});
            skLineSegment(sketch, "E102.3.36", {"start": v(-167.79, 10.5) * mm, "end": v(-167.79, 9.5) * mm});
            skArc(sketch, "E102.3.37", {"start": v(-184.88, -2) * mm, "mid": v(-186.73, -3.23) * mm, "end": v(-186.3, -5.41) * mm});
            skLineSegment(sketch, "E102.3.38", {"start": v(-199.83, 8.12) * mm, "end": v(-199.83, 11) * mm});
            skLineSegment(sketch, "E102.3.39", {"start": v(-182.83, 16.5) * mm, "end": v(-183.33, 16.5) * mm});
            skLineSegment(sketch, "E102.3.40", {"start": v(-201.95, 6) * mm, "end": v(-204.83, 6) * mm});
            skLineSegment(sketch, "E102.3.41", {"start": v(-165.83, 10.5) * mm, "end": v(-167.79, 10.5) * mm});
            skArc(sketch, "E102.3.42", {"start": v(-195.23, -24.43) * mm, "mid": v(-193.06, -24.84) * mm, "end": v(-191.83, -23) * mm});
            skArc(sketch, "E102.3.43", {"start": v(-205.83, 17) * mm, "mid": v(-207.74, 16.62) * mm, "end": v(-209.37, 15.54) * mm});
            skLineSegment(sketch, "E102.3.44", {"start": v(-204.33, -26.04) * mm, "end": v(-203.33, -26.04) * mm});
            skLineSegment(sketch, "E102.3.45", {"start": v(-182.83, 17) * mm, "end": v(-182.83, 16.5) * mm});
            skLineSegment(sketch, "E102.3.46", {"start": v(-173.83, 16.5) * mm, "end": v(-173.83, 17) * mm});
            skLineSegment(sketch, "E102.3.47", {"start": v(-204.33, -28) * mm, "end": v(-204.33, -26.04) * mm});
            skArc(sketch, "E102.3.48", {"start": v(-191.83, -8.95) * mm, "mid": v(-190.6, -7.1) * mm, "end": v(-188.42, -7.54) * mm});
            skLineSegment(sketch, "E102.3.49", {"start": v(-210.83, -11) * mm, "end": v(-210.33, -11) * mm});
            skLineSegment(sketch, "E102.3.50", {"start": v(-210.33, -20) * mm, "end": v(-210.83, -20) * mm});
            skLineSegment(sketch, "E102.3.51", {"start": v(-210.33, -0.5) * mm, "end": v(-210.33, 0) * mm});
            skLineSegment(sketch, "E102.3.52", {"start": v(-210.33, 0) * mm, "end": v(-210.83, 0) * mm});
            skLineSegment(sketch, "E102.3.53", {"start": v(-193.33, 16.5) * mm, "end": v(-193.83, 16.5) * mm});
            skLineSegment(sketch, "E102.3.54", {"start": v(-193.83, 16.5) * mm, "end": v(-193.83, 17) * mm});
            skPoint(sketch, "E102.center", {"position": v(-165.83, -28) * mm});
            skLineSegment(sketch, "E102.anchor1", {"start": v(-165.83, -28) * mm, "end": v(-165.83, 16.5) * mm, "construction": true});
            skLineSegment(sketch, "E102.anchor2", {"start": v(-165.83, -28) * mm, "end": v(-210.33, -28) * mm, "construction": true});
            skSolve(sketch);
        }
        {
            var Q0;
            Q0=makeQuery(id+"F0.imprint","IMPRINT",FACE,{"disambiguationData":[TD([[makeQuery(id+"F0.imprint","IMPRINT",EDGE,{"derivedFrom":sQuery(id+"F0.wireOp",EDGE,"E46.1.0")}),1.0]])]});
            var Q1;
            Q1=makeQuery(id+"F0.imprint","IMPRINT",FACE,{"disambiguationData":[TD([[makeQuery(id+"F0.imprint","IMPRINT",EDGE,{"derivedFrom":sQuery(id+"F0.wireOp",EDGE,"E0")}),1.0]])]});
            var Q2;
            Q2=makeQuery(id+"F0.imprint","IMPRINT",FACE,{"disambiguationData":[TD([[makeQuery(id+"F0.imprint","IMPRINT",EDGE,{"derivedFrom":sQuery(id+"F0.wireOp",EDGE,"E46.2.0")}),1.0]])]});
            var Q3;
            Q3=makeQuery(id+"F0.imprint","IMPRINT",FACE,{"disambiguationData":[TD([[makeQuery(id+"F0.imprint","IMPRINT",EDGE,{"derivedFrom":sQuery(id+"F0.wireOp",EDGE,"E46.3.0")}),1.0]])]});
            extrude(context, id + "F1", {"entities" : qUnion([Q0, Q1, Q2, Q3]), "offsetDistance" : 25 * mm, "depth" : 200 * mm});
        }
    });
